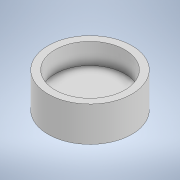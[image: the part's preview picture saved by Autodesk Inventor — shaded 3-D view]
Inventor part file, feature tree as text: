
AUTODESK INVENTOR PART (.ipt)
format: ipt  version: 2021 (Build 250183000, 183)  size: 105,472 bytes
history: native  units: in
note: dims shown in document units (in); Inventor stores cm internally (conversion verified against a paired STEP export)
features: extrude x2, sketch x2
ambient origin geometry x8: Origin, YZ Plane, XZ Plane, XY Plane, X Axis, Y Axis, Z Axis, Center Point
bodies: Solid1 (feature_tree)
feature tree (4):
  extrude  "Extrusion1"  Depth=0.3937in
  extrude  "Extrusion2"  Depth=0.0787in TaperAngle=0.0deg
  sketch  "Sketch1"  dims[d0=0.3937in d1=0.4724in]
  sketch  "Sketch2"  dims[d2=0.1181in d3=0.0in d4=0.0787in d5=0.0in]
